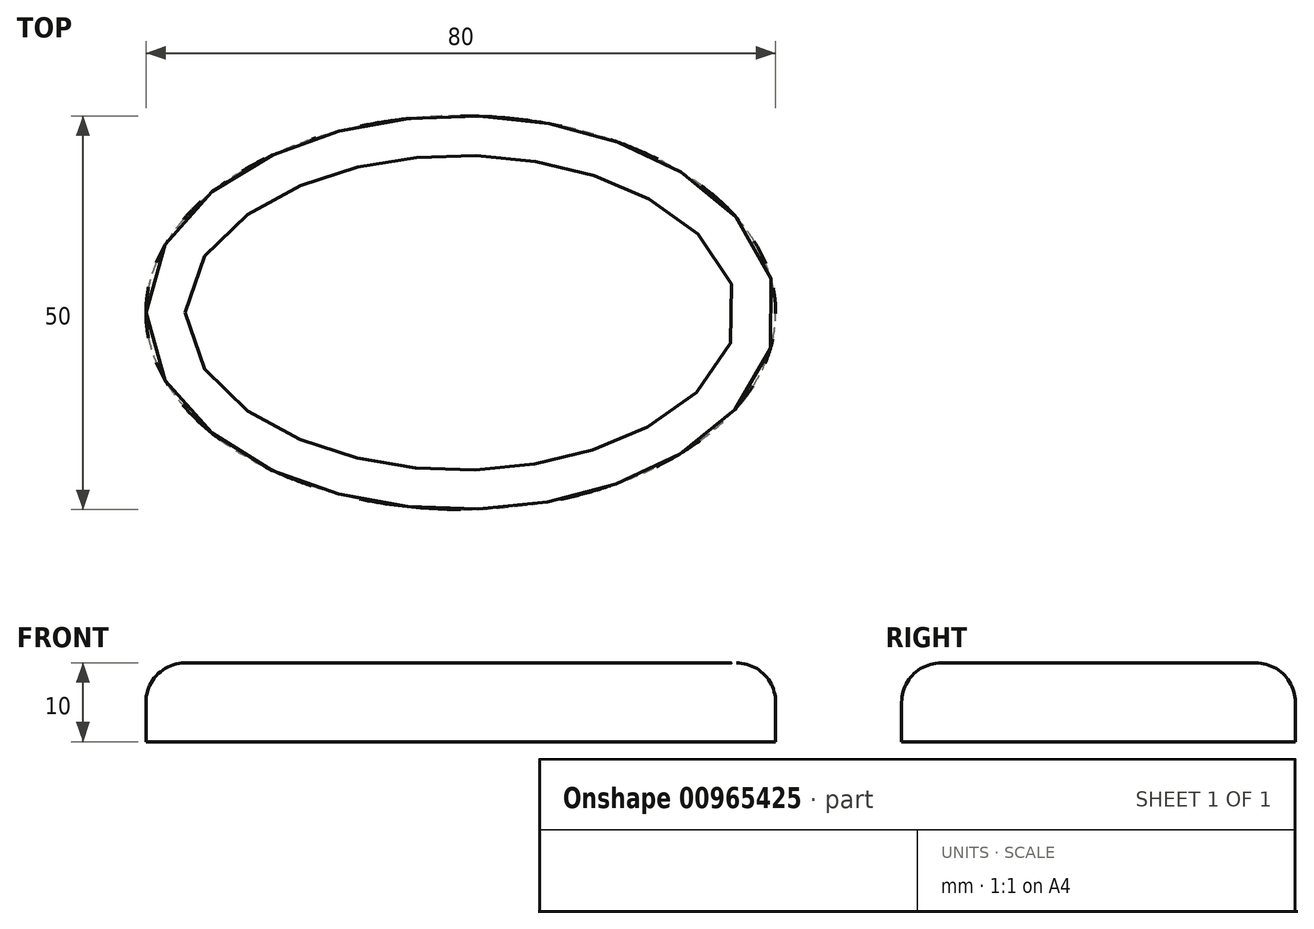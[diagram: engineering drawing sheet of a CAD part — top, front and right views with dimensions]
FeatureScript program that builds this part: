
annotation { "Feature Type Name" : "Feature", "Feature Type Description" : "" }
export const myFeature = defineFeature(function(context is Context, id is Id, definition is map)
    precondition{}
    {
        {
            var Q0;
            Q0=qCreatedBy(makeId("Top.planeOp"),FACE);
            var sketch = newSketch(context, id + "F0", { "sketchPlane" : qUnion([Q0])});
            skEllipse(sketch, "E0", {"center": v(0, 0) * mm, "majorRadius": 40 * mm, "minorRadius": 25 * mm, "majorAxis": v(-1, 0)});
            skSolve(sketch);
        }
        {
            var Q0;
            Q0=makeQuery(id+"F0.imprint","IMPRINT",FACE,{"disambiguationData":[TD([[makeQuery(id+"F0.imprint","IMPRINT",EDGE,{"derivedFrom":sQuery(id+"F0.wireOp",EDGE,"E0")}),1.0]])]});
            extrude(context, id + "F1", {"entities" : qUnion([Q0]), "depth" : 10 * mm, "offsetDistance" : 25 * mm});
        }
        {
            var Q0;
            Q0=makeQuery(id+"F1.opExtrude","CAP_EDGE",EDGE,{"disambiguationData":[OSD([sQuery(id+"F0.wireOp",EDGE,"E0")])],"isStart":false});
            fillet(context, id + "F2", {"entities" : qUnion([Q0]), "radius" : 5 * mm, "tangentPropagation" : true, "allowEdgeOverflow" : false});
        }
    });
